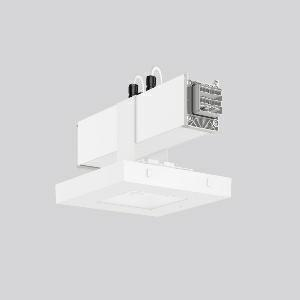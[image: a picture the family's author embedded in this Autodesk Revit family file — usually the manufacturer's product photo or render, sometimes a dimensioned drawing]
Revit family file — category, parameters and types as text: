
# Revit family: linedo_module_rw_9503rw_762_409_100_9a47
name_source: partatom
category: Lighting Fixtures
units: mm (PartAtom-declared; Revit-internal decimal feet)

## family parameters
Cut with Voids When Loaded = No
Host = Face
Light Source = No
Part Type = Normal
Room Calculation Point = No
Round Connector Dimension = Use Diameter
Shared = No

## types (1)
- LINEDO Module RW (1 x LED Modul 765, 190 lm, 6500)
    Apparent Load = 4 VA
    CIE Flux Codes = 39 73 100 100 100
    Color Rendering = 70
    Color Temperature = 6500
    Default Elevation = 1800 mm
    Description = LINEDO, 4,2 W, 190 lm, 765, white, on/off
Continuous line luminaire, L 330 B 198 H 170, CBS, emergency-190 lm, AC-Control
    Height = 170 mm  [stored 0.557743 ft]
    Lamp = 1 x LED Modul 765
    Lamp Light Flux = 190 lm
    Lamp count = 1
    Length = 330 mm
    Lifetime = 50000 h
    Luminous efficacy = 45 lm/W
    Manufacturer = RZB
    ModVariant = No
    Model = 9503RW.762.409.100
    Mounting Place = Ceiling
    Mounting Type = Surface mounted, Pendant
    Number of Poles = 1
    OnlyDefault = Yes
    Power Factor = 1
    Product Name = LINEDO Module RW
    Product group = Continuous line luminaire system Linedo IP 54
    ProductGroupID = 314
    Protection Class = Protection class I
    Protection Degree = IP 54
    RLX_Detail_Level = 1
    RLX_Emergency_Light_Flux = 190 lm
    RLX_Emergency_Type = 3
    RLX_Emergency_Type_DB = Yes
    RlxData = <blob elided: 29421 chars, md5=aaddf5c4>
    Socket = socket
    Standby Power = 0 W
    System Light Flux = 190 lm
    System Power = 4 W
    Type Comments = Product without accessories
    Type Image = 9503rw.762.434.000.jpg
    URL = http://relux.com
    VarID = ---
    Voltage = 230 V
    Voltage Range = 220-240 V
    Weight = 0.00 kg
    Width = 198 mm

note: [stored X ft] marks values corroborated as IEEE doubles in the binary element streams (Revit-internal decimal feet)

## geometry (parser evidence)
native form markers: Blend x4, Sweep x13
no freeform markers — native parametric forms only
